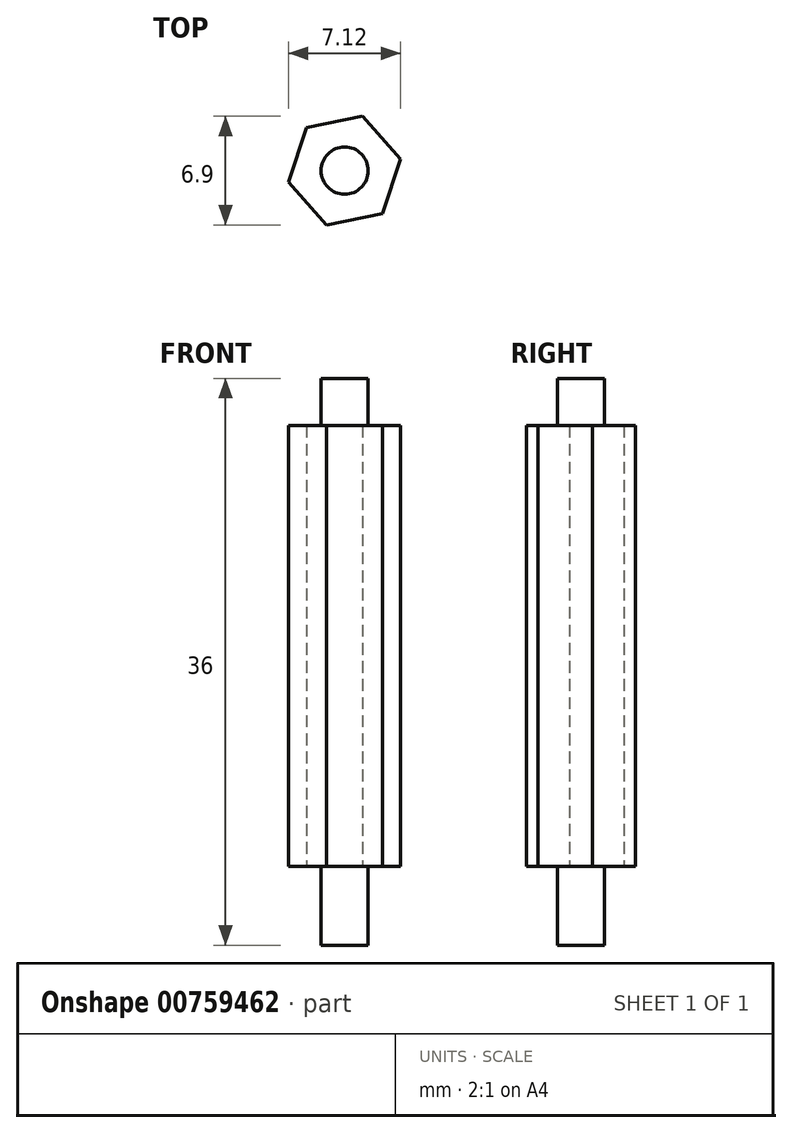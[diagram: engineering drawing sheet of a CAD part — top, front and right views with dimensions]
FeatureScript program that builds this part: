
annotation { "Feature Type Name" : "Feature", "Feature Type Description" : "" }
export const myFeature = defineFeature(function(context is Context, id is Id, definition is map)
    precondition{}
    {
        {
            var Q0;
            Q0=qCreatedBy(makeId("Top.planeOp"),FACE);
            var sketch = newSketch(context, id + "F0", { "sketchPlane" : qUnion([Q0])});
            skCircle(sketch, "E0.cCircle", {"center": v(0, 0) * mm, "radius": 3.15 * mm, "construction": true});
            skLineSegment(sketch, "E0.0", {"start": v(3.56, 0.73) * mm, "end": v(2.41, -2.72) * mm});
            skLineSegment(sketch, "E0.1", {"start": v(2.41, -2.72) * mm, "end": v(-1.15, -3.45) * mm});
            skLineSegment(sketch, "E0.2", {"start": v(-1.15, -3.45) * mm, "end": v(-3.56, -0.73) * mm});
            skLineSegment(sketch, "E0.3", {"start": v(-3.56, -0.73) * mm, "end": v(-2.41, 2.72) * mm});
            skLineSegment(sketch, "E0.4", {"start": v(-2.41, 2.72) * mm, "end": v(1.15, 3.45) * mm});
            skLineSegment(sketch, "E0.5", {"start": v(1.15, 3.45) * mm, "end": v(3.56, 0.73) * mm});
            skPoint(sketch, "E0.0.midPoint", {"position": v(2.99, -1) * mm});
            skCircle(sketch, "E1", {"center": v(0, 0) * mm, "radius": 1.5 * mm});
            skSolve(sketch);
        }
        {
            var Q0;
            Q0=makeQuery(id+"F0.imprint","IMPRINT",FACE,{"disambiguationData":[TD([[makeQuery(id+"F0.imprint","IMPRINT",EDGE,{"derivedFrom":sQuery(id+"F0.wireOp",EDGE,"E0.0")}),-1.0]])]});
            var Q1;
            Q1=makeQuery(id+"F0.imprint","IMPRINT",FACE,{"disambiguationData":[TD([[makeQuery(id+"F0.imprint","IMPRINT",EDGE,{"derivedFrom":sQuery(id+"F0.wireOp",EDGE,"E1")}),1.0]])]});
            extrude(context, id + "F1", {"entities" : qUnion([Q0, Q1]), "depth" : 28 * mm, "offsetDistance" : 25 * mm});
        }
        {
            var Q0;
            Q0=makeQuery(id+"F0.imprint","IMPRINT",FACE,{"disambiguationData":[TD([[makeQuery(id+"F0.imprint","IMPRINT",EDGE,{"derivedFrom":sQuery(id+"F0.wireOp",EDGE,"E1")}),1.0]])]});
            extrude(context, id + "F2", {"entities" : qUnion([Q0]), "operationType" : NewBodyOperationType.ADD, "oppositeDirection" : true, "depth" : 5 * mm, "offsetDistance" : 25 * mm});
        }
        {
            var Q0;
            Q0=makeQuery(id+"F1.opExtrude","CAP_FACE",FACE,{"disambiguationData":[OSD([sQuery(id+"F0.wireOp",EDGE,"E0.0"),sQuery(id+"F0.wireOp",EDGE,"E0.1"),sQuery(id+"F0.wireOp",EDGE,"E0.2"),sQuery(id+"F0.wireOp",EDGE,"E0.3"),sQuery(id+"F0.wireOp",EDGE,"E0.4"),sQuery(id+"F0.wireOp",EDGE,"E0.5")])],"isStart":false});
            var sketch = newSketch(context, id + "F3", { "sketchPlane" : qUnion([Q0])});
            skCircle(sketch, "E2", {"center": v(0, 0) * mm, "radius": 1.5 * mm});
            skSolve(sketch);
        }
        {
            var Q0;
            Q0=makeQuery(id+"F3.imprint","IMPRINT",FACE,{"disambiguationData":[TD([[makeQuery(id+"F3.imprint","IMPRINT",EDGE,{"derivedFrom":sQuery(id+"F3.wireOp",EDGE,"E2")}),1.0]])]});
            extrude(context, id + "F4", {"entities" : qUnion([Q0]), "operationType" : NewBodyOperationType.ADD, "depth" : 3 * mm, "offsetDistance" : 25 * mm});
        }
    });
